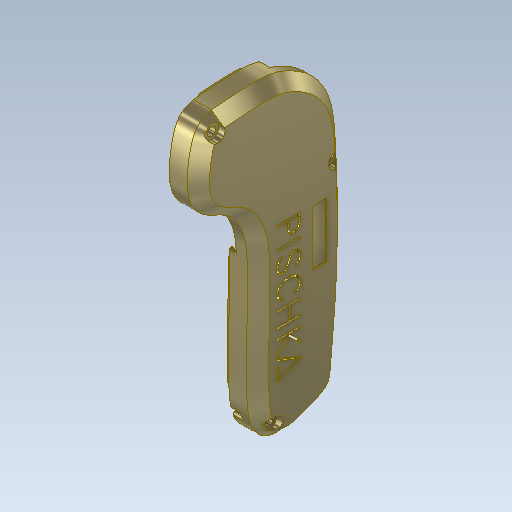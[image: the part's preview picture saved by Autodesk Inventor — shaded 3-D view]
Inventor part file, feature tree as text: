
AUTODESK INVENTOR PART (.ipt)
format: ipt  version: 2020.1 (Build 241239000, 239)  size: 1,649,664 bytes
history: native  units: mm
features: reference x20, extrude x18, sketch x12, other x8, projected_geometry x7, chamfer x6, plane x5, fillet x3, shell x1, emboss x1
ambient origin geometry x8: Origin, YZ Plane, XZ Plane, XY Plane, X Axis, Y Axis, Z Axis, Center Point
bodies: Solid1 (feature_tree)
feature tree (81):
  other  "Outline"
  other  "Acceleration Knob"
  extrude  "Extrusion1"  Depth=33.5mm
  chamfer  "Chamfer1"  Distance=200.0mm Angle=360.0deg
  shell  "Shell1"  Thickness=12.0mm
  extrude  "Extrusion2"  Depth=1.5mm
  plane  "Work Plane1"
  extrude  "Extrusion4"  Depth=4.2mm TaperAngle=0.0deg
  chamfer  "Chamfer2"  Distance=3.2mm
  plane  "Work Plane3"
  sketch  "Sketch8"  dims[d87=31.0mm d88=200.0mm d90=360.0deg d94=12.0mm d95=0.0mm]
  plane  "Work Plane4"
  extrude  "Extrusion5"  Depth=6.4mm
  plane  "Work Plane5"
  extrude  "Extrusion6"  Depth=9.0mm
  extrude  "Extrusion7"  Depth=10.0mm TaperAngle=0.0deg
  extrude  "Extrusion8"  Depth=10.0mm
  extrude  "Extrusion9"  Depth=4.5mm
  chamfer  "Chamfer4"  Distance=4.5mm
  fillet  "Fillet1"  Radius=4.5mm
  fillet  "Fillet2"  Radius=1.5mm
  extrude  "Extrusion10"  Depth=3.5mm
  extrude  "Extrusion11"  Depth=3.5mm
  sketch  "Sketch17"  dims[d113=1.0mm d114=2.0mm d115=45.0deg d119=6.4mm]
  extrude  "Extrusion12"  Depth=3.5mm
  extrude  "Extrusion13"  Depth=10.0mm TaperAngle=0.0deg
  extrude  "Extrusion14"  Depth=4.0mm TaperAngle=0.0deg
  extrude  "Extrusion15"  Depth=10.5mm
  chamfer  "Chamfer5"  Distance=26.2mm
  sketch  "Sketch18"  dims[d121=2.6mm d122=9.0mm]
  extrude  "Extrusion16"  Depth=12.0mm
  extrude  "Extrusion17"  Depth=30.0mm
  chamfer  "Chamfer6"  Distance=3.0mm
  fillet  "Fillet3"  Radius=0.536mm
  emboss  "Emboss1"
  plane  "Work Plane6"
  extrude  "Extrusion18"  Depth=0.5mm
  chamfer  "Chamfer7"  Distance=1.0mm
  extrude  "Extrusion19"  Depth=10.0mm TaperAngle=0.0deg
  other  "Image1"
  sketch  "Sketch5"  dims[d0=131.0mm d86=33.5mm]
  reference  "Reference1"
  reference  "Reference2"
  reference  "Reference3"
  reference  "Reference4"
  reference  "Reference5"
  reference  "Reference6"
  reference  "Reference7"
  sketch  "Sketch9"  dims[d96=4.6mm d97=2.0mm d98=45.0deg d99=1.5mm]
  sketch  "Sketch10"  dims[d103=0.35mm d104=4.2mm d105=0.0mm]
  reference  "Reference8"
  reference  "Reference9"
  reference  "Reference10"
  reference  "Reference11"
  reference  "Reference12"
  reference  "Reference13"
  reference  "Reference14"
  reference  "Reference15"
  reference  "Reference16"
  reference  "Reference17"
  reference  "Reference18"
  reference  "Reference19"
  reference  "Reference20"
  sketch  "Sketch13"  dims[d108=2.6mm]
  sketch  "Sketch15"  dims[d109=6.5mm]
  sketch  "Sketch16"  dims[d110=22.0mm d111=3.2mm d112=0.0mm]
  sketch  "Sketch19"  dims[d123=10.0mm d124=10.0mm d125=0.0mm]
  sketch  "Sketch20"  dims[d126=-3.8mm d127=10.0mm]
  sketch  "Sketch21"  dims[d128=10.0mm d129=0.0mm d130=4.5mm d131=4.5mm d132=4.5mm d133=1.5mm d134=3.5mm d135=3.5mm d136=3.5mm d137=10.0mm d138=0.0mm d139=4.0mm d140=0.0mm d145=10.5mm d146=26.2mm d147=12.0mm d149=30.0mm d150=3.0mm d151=0.0mm d155=0.536mm d156=1.5mm d157=45.0deg d160=0.5mm d161=1.0mm d162=10.0mm d163=0.0mm d164=6.1mm d165=2.55mm d166=0.0mm d167=22.8mm d168=5.8mm d169=7.11mm d170=4.5mm d171=38.0mm d172=3.0mm d173=1.5mm d174=2.0mm d175=1.2mm d176=2.55mm d177=0.0mm d178=1.0mm d179=0.0mm d180=1.0mm d181=0.0mm d182=1.0mm d183=0.0mm d184=1.0mm d185=2.0mm d186=45.0deg d187=12.0mm d188=1.2mm d189=1.2mm d193=2.9mm d194=0.8mm d195=0.8mm d196=0.8mm d197=0.8mm d198=0.8mm d199=1.0mm d200=0.0mm d201=2.0mm d202=0.0mm d203=2.0mm d204=2.0mm d205=45.0deg d206=1.0mm d368=1.0mm d369=0.0mm d371=7.3mm d372=10.0mm d373=1.745329mm d374=3.0mm d375=0.25mm d376=2.0mm d377=45.0deg d378=12.0mm d379=60.0mm d380=56.119884mm d381=28.059942mm d382=0.5mm d383=0.0mm]
  projected_geometry  "Projected Loop1"
  projected_geometry  "Projected Loop2"
  projected_geometry  "Projected Loop3"
  projected_geometry  "Projected Loop4"
  projected_geometry  "Projected Loop5"
  projected_geometry  "Projected Loop6"
  projected_geometry  "Projected Loop7"
  parser-record x1  (decoder bookkeeping rows leaked as tree rows — omitted from the tree; the rows remain in map.json)
  other  "Remote.iam"
  other  "Trigger:1"
  other  "Knob_v2:1"
  other  "Remote Bottom Shell:1"
note: 1 file-system path scrubbed to <path> (originals preserved in map.json)
